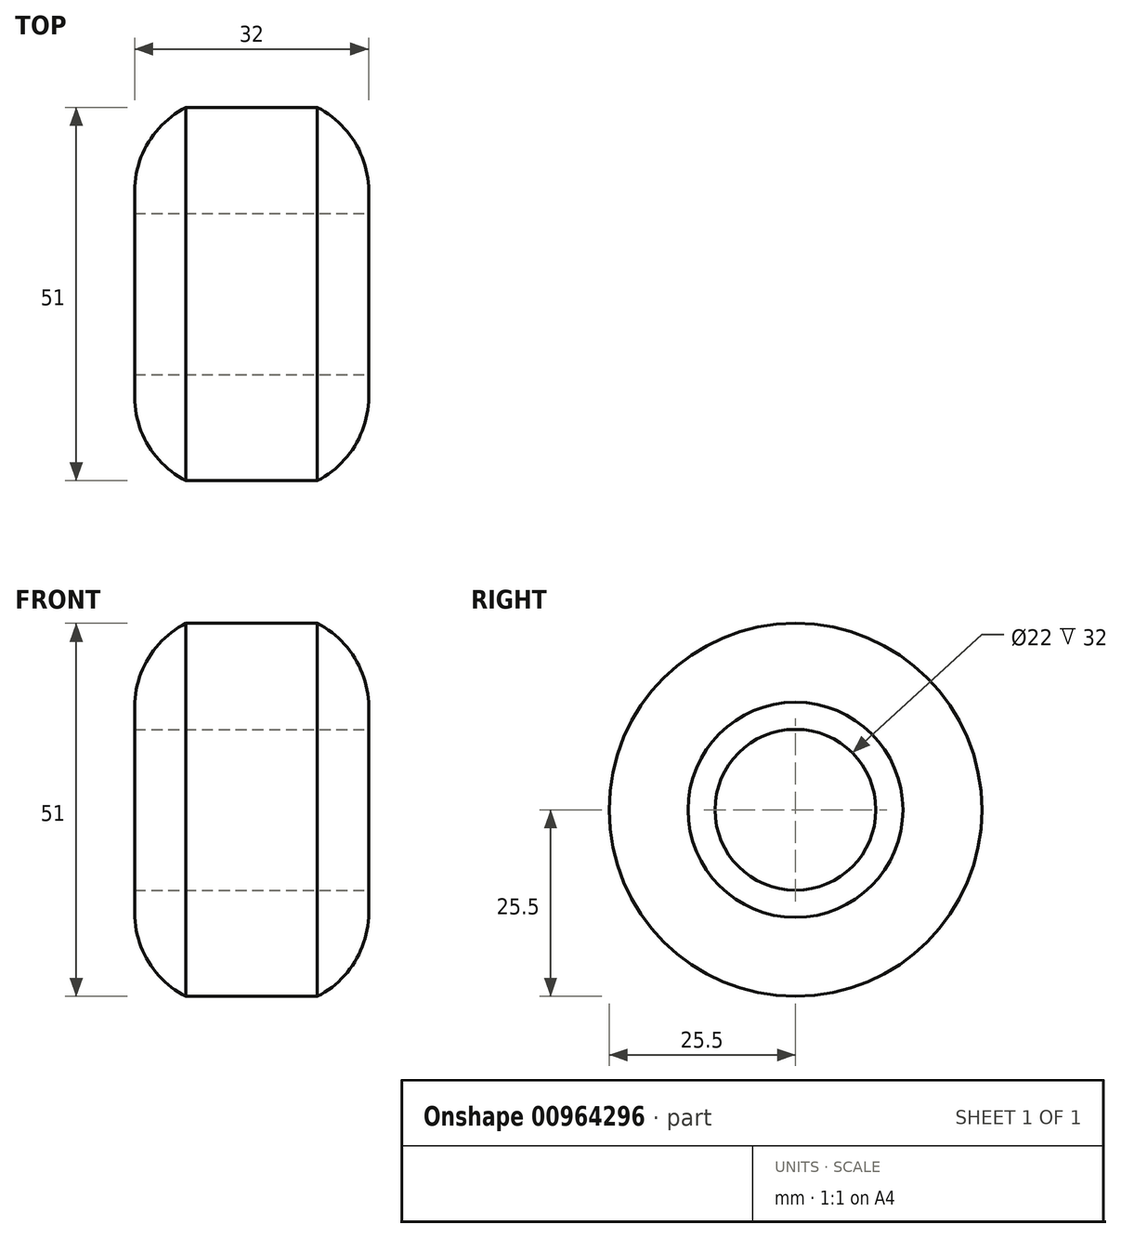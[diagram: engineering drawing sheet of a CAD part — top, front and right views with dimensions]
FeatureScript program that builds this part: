
annotation { "Feature Type Name" : "Feature", "Feature Type Description" : "" }
export const myFeature = defineFeature(function(context is Context, id is Id, definition is map)
    precondition{}
    {
        {
            var Q0;
            Q0=qCreatedBy(makeId("Front.planeOp"),FACE);
            var sketch = newSketch(context, id + "F0", { "sketchPlane" : qUnion([Q0])});
            skLineSegment(sketch, "E0.bottom", {"start": v(0, 0) * mm, "end": v(16, 0) * mm});
            skLineSegment(sketch, "E0.top", {"start": v(0, 25.5) * mm, "end": v(9, 25.5) * mm});
            skLineSegment(sketch, "E0.left", {"start": v(0, 0) * mm, "end": v(0, 25.5) * mm, "construction": true});
            skArc(sketch, "E1", {"start": v(16, 14.7) * mm, "mid": v(13.93, 21.03) * mm, "end": v(9, 25.5) * mm});
            skLineSegment(sketch, "E2", {"start": v(16, 14.7) * mm, "end": v(16, 0) * mm});
            skLineSegment(sketch, "E3.MirrorCS", {"start": v(0, 25.5) * mm, "end": v(-9, 25.5) * mm});
            skArc(sketch, "E4.MirrorCS", {"start": v(-16, 14.7) * mm, "mid": v(-13.93, 21.03) * mm, "end": v(-9, 25.5) * mm});
            skLineSegment(sketch, "E5.MirrorCS", {"start": v(-16, 14.7) * mm, "end": v(-16, 0) * mm});
            skLineSegment(sketch, "E6.MirrorCS", {"start": v(0, 0) * mm, "end": v(-16, 0) * mm});
            skSolve(sketch);
        }
        {
            var Q0;
            Q0 = qSketchRegion(id + "F0", true);
            var Q1;
            Q1=sQuery(id+"F0.wireOp",EDGE,"E0.bottom");
            revolve(context, id + "F1", {"surfaceOperationType" : NewSurfaceOperationType.NEW, "entities" : qUnion([Q0]), "axis" : qUnion([Q1]), "revolveType" : RevolveType.FULL});
        }
        {
            var Q0;
            Q0=makeQuery(id+"F1.opRevolve","SWEPT_FACE",FACE,{"disambiguationData":[OSD([sQuery(id+"F0.wireOp",EDGE,"E2")])]});
            var sketch = newSketch(context, id + "F2", { "sketchPlane" : qUnion([Q0])});
            skCircle(sketch, "E7", {"center": v(0, 0) * mm, "radius": 11 * mm});
            skSolve(sketch);
        }
        {
            var Q0;
            Q0 = qSketchRegion(id + "F2", true);
            extrude(context, id + "F3", {"entities" : qUnion([Q0]), "operationType" : NewBodyOperationType.REMOVE, "endBound" : BoundingType.THROUGH_ALL, "oppositeDirection" : true, "depth" : 25 * mm, "offsetDistance" : 25 * mm});
        }
    });
